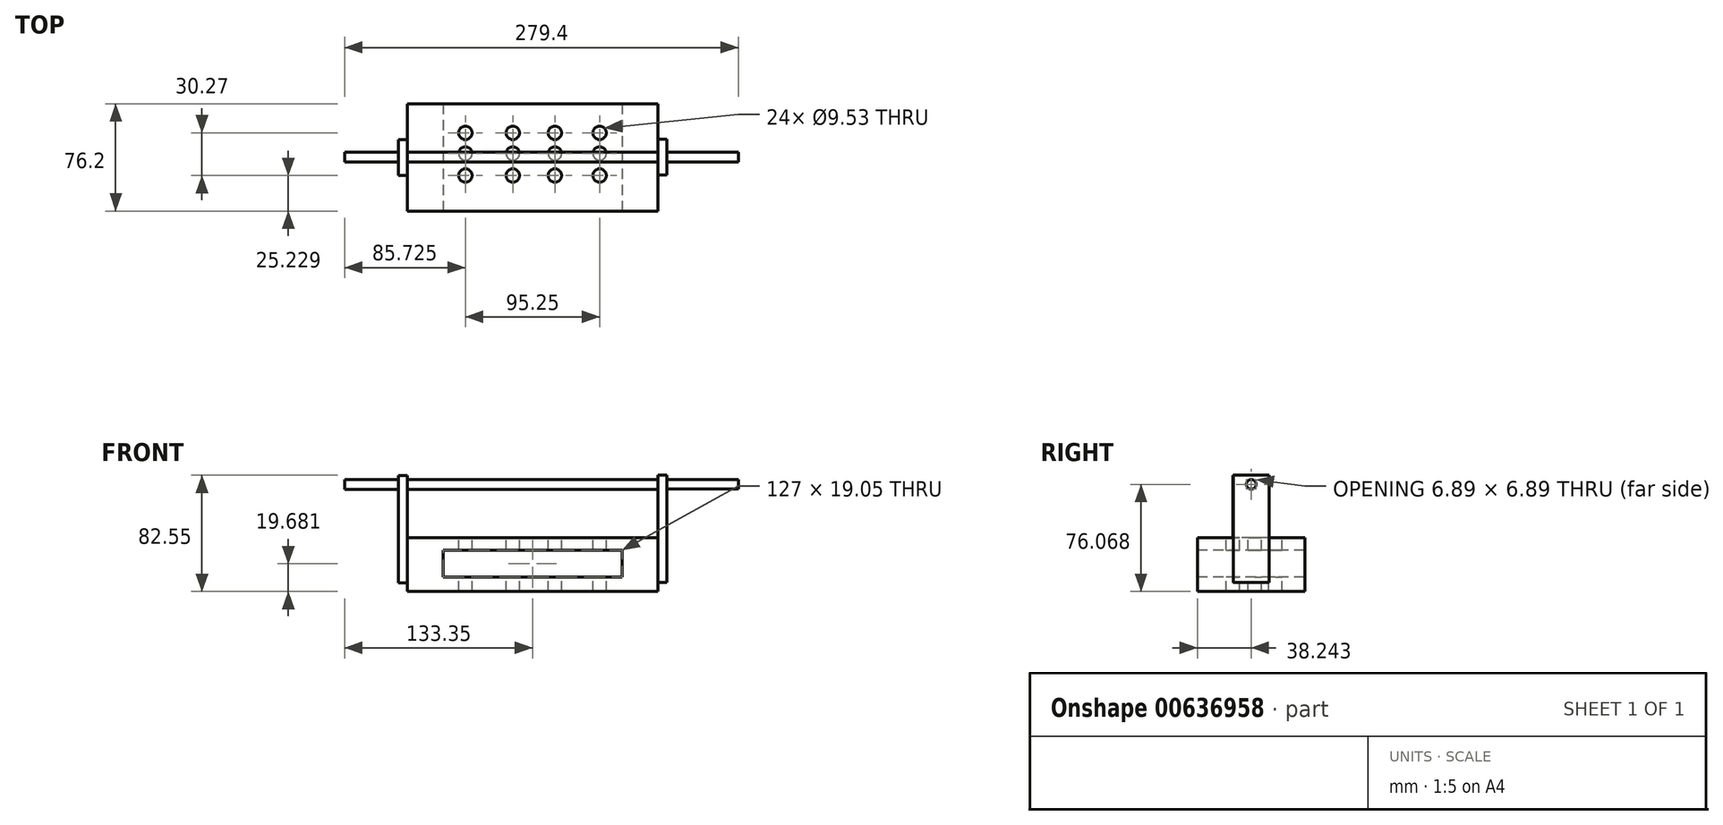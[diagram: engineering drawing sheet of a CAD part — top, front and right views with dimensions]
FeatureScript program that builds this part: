
annotation { "Feature Type Name" : "Feature", "Feature Type Description" : "" }
export const myFeature = defineFeature(function(context is Context, id is Id, definition is map)
    precondition{}
    {
        {
            var Q0;
            Q0=qCreatedBy(makeId("Front.planeOp"),FACE);
            var sketch = newSketch(context, id + "F0", { "sketchPlane" : qUnion([Q0])});
            skLineSegment(sketch, "E0", {"start": v(0, 0) * mm, "end": v(177.8, 0) * mm});
            skLineSegment(sketch, "E1", {"start": v(177.8, 0) * mm, "end": v(177.8, 38.1) * mm});
            skLineSegment(sketch, "E2", {"start": v(177.8, 38.1) * mm, "end": v(0, 38.1) * mm});
            skLineSegment(sketch, "E3", {"start": v(0, 38.1) * mm, "end": v(0, 0) * mm});
            skSolve(sketch);
        }
        {
            var Q0;
            Q0 = qSketchRegion(id + "F0", true);
            extrude(context, id + "F1", {"entities" : qUnion([Q0]), "oppositeDirection" : true, "depth" : 76.2 * mm, "offsetDistance" : 25.4 * mm});
        }
        {
            var Q0;
            Q0=makeQuery(id+"F1.opExtrude","SWEPT_FACE",FACE,{"disambiguationData":[OSD([sQuery(id+"F0.wireOp",EDGE,"E1")])]});
            var sketch = newSketch(context, id + "F2", { "sketchPlane" : qUnion([Q0])});
            skLineSegment(sketch, "E4", {"start": v(25.54, 6.35) * mm, "end": v(50.94, 6.35) * mm});
            skLineSegment(sketch, "E5", {"start": v(38.1, 6.35) * mm, "end": v(25.54, 6.35) * mm});
            skLineSegment(sketch, "E6", {"start": v(50.94, 6.35) * mm, "end": v(50.94, 82.55) * mm});
            skLineSegment(sketch, "E7", {"start": v(50.94, 82.55) * mm, "end": v(25.54, 82.55) * mm});
            skLineSegment(sketch, "E8", {"start": v(25.54, 82.55) * mm, "end": v(25.54, 6.35) * mm});
            skSolve(sketch);
        }
        {
            var Q0;
            Q0 = qSketchRegion(id + "F2", true);
            extrude(context, id + "F3", {"entities" : qUnion([Q0]), "operationType" : NewBodyOperationType.ADD, "depth" : 6.35 * mm, "offsetDistance" : 25.4 * mm});
        }
        {
            var Q0;
            Q0=makeQuery(id+"F1.opExtrude","SWEPT_FACE",FACE,{"disambiguationData":[OSD([sQuery(id+"F0.wireOp",EDGE,"E3")])]});
            var sketch = newSketch(context, id + "F4", { "sketchPlane" : qUnion([Q0])});
            skLineSegment(sketch, "E9", {"start": v(-50.63, 6.23) * mm, "end": v(-25.23, 6.23) * mm});
            skLineSegment(sketch, "E10", {"start": v(-38.07, 6.23) * mm, "end": v(-50.63, 6.23) * mm});
            skLineSegment(sketch, "E11", {"start": v(-25.23, 6.23) * mm, "end": v(-25.23, 82.43) * mm});
            skLineSegment(sketch, "E12", {"start": v(-25.23, 82.43) * mm, "end": v(-50.63, 82.43) * mm});
            skLineSegment(sketch, "E13", {"start": v(-50.63, 82.43) * mm, "end": v(-50.63, 6.23) * mm});
            skSolve(sketch);
        }
        {
            var Q0;
            Q0 = qSketchRegion(id + "F4", true);
            extrude(context, id + "F5", {"entities" : qUnion([Q0]), "operationType" : NewBodyOperationType.ADD, "depth" : 6.35 * mm, "offsetDistance" : 25.4 * mm});
        }
        {
            var Q0;
            Q0=makeQuery(id+"F1.opExtrude","CAP_FACE",FACE,{"disambiguationData":[OSD([sQuery(id+"F0.wireOp",EDGE,"E0"),sQuery(id+"F0.wireOp",EDGE,"E1"),sQuery(id+"F0.wireOp",EDGE,"E2"),sQuery(id+"F0.wireOp",EDGE,"E3")])],"isStart":true});
            var sketch = newSketch(context, id + "F6", { "sketchPlane" : qUnion([Q0])});
            skLineSegment(sketch, "E14", {"start": v(25.4, 19.68) * mm, "end": v(25.4, 10.16) * mm});
            skLineSegment(sketch, "E15", {"start": v(25.4, 10.16) * mm, "end": v(152.4, 10.16) * mm});
            skLineSegment(sketch, "E16", {"start": v(152.4, 10.16) * mm, "end": v(152.4, 19.68) * mm});
            skLineSegment(sketch, "E17", {"start": v(152.4, 19.68) * mm, "end": v(152.4, 29.2) * mm});
            skLineSegment(sketch, "E18", {"start": v(152.4, 29.2) * mm, "end": v(25.4, 29.2) * mm});
            skLineSegment(sketch, "E19", {"start": v(25.4, 29.2) * mm, "end": v(25.4, 19.68) * mm});
            skPoint(sketch, "E20.start.orphan", {"position": v(0, 19.05) * mm});
            skPoint(sketch, "E21.end.orphan", {"position": v(177.8, 19.05) * mm});
            skPoint(sketch, "E22.end.orphan", {"position": v(88.9, 29.2) * mm});
            skPoint(sketch, "E22.start.orphan", {"position": v(88.9, 10.16) * mm});
            skSolve(sketch);
        }
        {
            var Q0;
            Q0 = qSketchRegion(id + "F6", true);
            extrude(context, id + "F7", {"entities" : qUnion([Q0]), "operationType" : NewBodyOperationType.REMOVE, "oppositeDirection" : true, "depth" : 76.2 * mm, "offsetDistance" : 25.4 * mm});
        }
        {
            var Q0;
            Q0=makeQuery(id+"F3.opExtrude","CAP_FACE",FACE,{"disambiguationData":[OSD([sQuery(id+"F2.wireOp",EDGE,"E4"),sQuery(id+"F2.wireOp",EDGE,"E6"),sQuery(id+"F2.wireOp",EDGE,"E7"),sQuery(id+"F2.wireOp",EDGE,"E8")])],"isStart":false});
            var sketch = newSketch(context, id + "F8", { "sketchPlane" : qUnion([Q0])});
            skCircle(sketch, "E23", {"center": v(38.24, 76.07) * mm, "radius": 3.5 * mm});
            skPoint(sketch, "E23.centerSnap0", {"position": v(38.24, 82.55) * mm});
            skSolve(sketch);
        }
        {
            var Q0;
            Q0 = qSketchRegion(id + "F8", true);
            extrude(context, id + "F9", {"entities" : qUnion([Q0]), "operationType" : NewBodyOperationType.ADD, "oppositeDirection" : true, "depth" : 228.6 * mm, "offsetDistance" : 25.4 * mm});
        }
        {
            var Q0;
            Q0=makeQuery(id+"F1.opExtrude","SWEPT_FACE",FACE,{"disambiguationData":[OSD([sQuery(id+"F0.wireOp",EDGE,"E2")])]});
            var sketch = newSketch(context, id + "F10", { "sketchPlane" : qUnion([Q0])});
            skLineSegment(sketch, "E24", {"start": v(0, 59.82) * mm, "end": v(25.4, 59.82) * mm});
            skLineSegment(sketch, "E25", {"start": v(177.8, 59.82) * mm, "end": v(152.4, 59.82) * mm});
            skPoint(sketch, "E25.startSnap0", {"position": v(12.7, 59.82) * mm});
            skLineSegment(sketch, "E26", {"start": v(25.4, 59.82) * mm, "end": v(57.15, 59.82) * mm});
            skLineSegment(sketch, "E27", {"start": v(57.15, 59.82) * mm, "end": v(88.9, 59.82) * mm});
            skLineSegment(sketch, "E28", {"start": v(88.9, 59.82) * mm, "end": v(120.65, 59.82) * mm});
            skLineSegment(sketch, "E29", {"start": v(120.65, 59.82) * mm, "end": v(152.4, 59.82) * mm});
            skCircle(sketch, "E30", {"center": v(41.28, 55.5) * mm, "radius": 4.76 * mm});
            skPoint(sketch, "E30.centerSnap0", {"position": v(41.28, 59.82) * mm});
            skCircle(sketch, "E31", {"center": v(74.93, 55.5) * mm, "radius": 4.76 * mm});
            skCircle(sketch, "E32", {"center": v(104.78, 55.5) * mm, "radius": 4.76 * mm});
            skPoint(sketch, "E32.centerSnap0", {"position": v(104.78, 59.82) * mm});
            skCircle(sketch, "E33", {"center": v(136.53, 55.5) * mm, "radius": 4.76 * mm});
            skPoint(sketch, "E33.centerSnap0", {"position": v(136.53, 59.82) * mm});
            skCircle(sketch, "E34", {"center": v(41.28, 40.81) * mm, "radius": 4.76 * mm});
            skCircle(sketch, "E35", {"center": v(74.93, 40.81) * mm, "radius": 4.76 * mm});
            skCircle(sketch, "E36", {"center": v(104.78, 40.81) * mm, "radius": 4.76 * mm});
            skCircle(sketch, "E37", {"center": v(136.53, 40.81) * mm, "radius": 4.76 * mm});
            skCircle(sketch, "E38", {"center": v(41.28, 25.23) * mm, "radius": 4.76 * mm});
            skLineSegment(sketch, "E39", {"start": v(0, 12.61) * mm, "end": v(0, 0) * mm});
            skCircle(sketch, "E40", {"center": v(74.93, 25.23) * mm, "radius": 4.76 * mm});
            skCircle(sketch, "E41", {"center": v(104.78, 25.23) * mm, "radius": 4.76 * mm});
            skCircle(sketch, "E42", {"center": v(136.53, 25.23) * mm, "radius": 4.76 * mm});
            skSolve(sketch);
        }
        {
            var Q0;
            Q0 = qSketchRegion(id + "F10", true);
            extrude(context, id + "F11", {"entities" : qUnion([Q0]), "operationType" : NewBodyOperationType.REMOVE, "oppositeDirection" : true, "depth" : 38.1 * mm, "offsetDistance" : 25.4 * mm});
        }
        {
            var Q0;
            Q0=makeQuery(id+"F9.opExtrude","CAP_FACE",FACE,{"disambiguationData":[OSD([sQuery(id+"F8.wireOp",EDGE,"E23")])],"isStart":false});
            var sketch = newSketch(context, id + "F12", { "sketchPlane" : qUnion([Q0])});
            skCircle(sketch, "E43", {"center": v(-38.24, 76.07) * mm, "radius": 3.44 * mm});
            skSolve(sketch);
        }
        {
            var Q0;
            Q0 = qSketchRegion(id + "F12", true);
            extrude(context, id + "F13", {"entities" : qUnion([Q0]), "operationType" : NewBodyOperationType.ADD, "oppositeDirection" : true, "depth" : 279.4 * mm, "offsetDistance" : 25.4 * mm});
        }
    });
